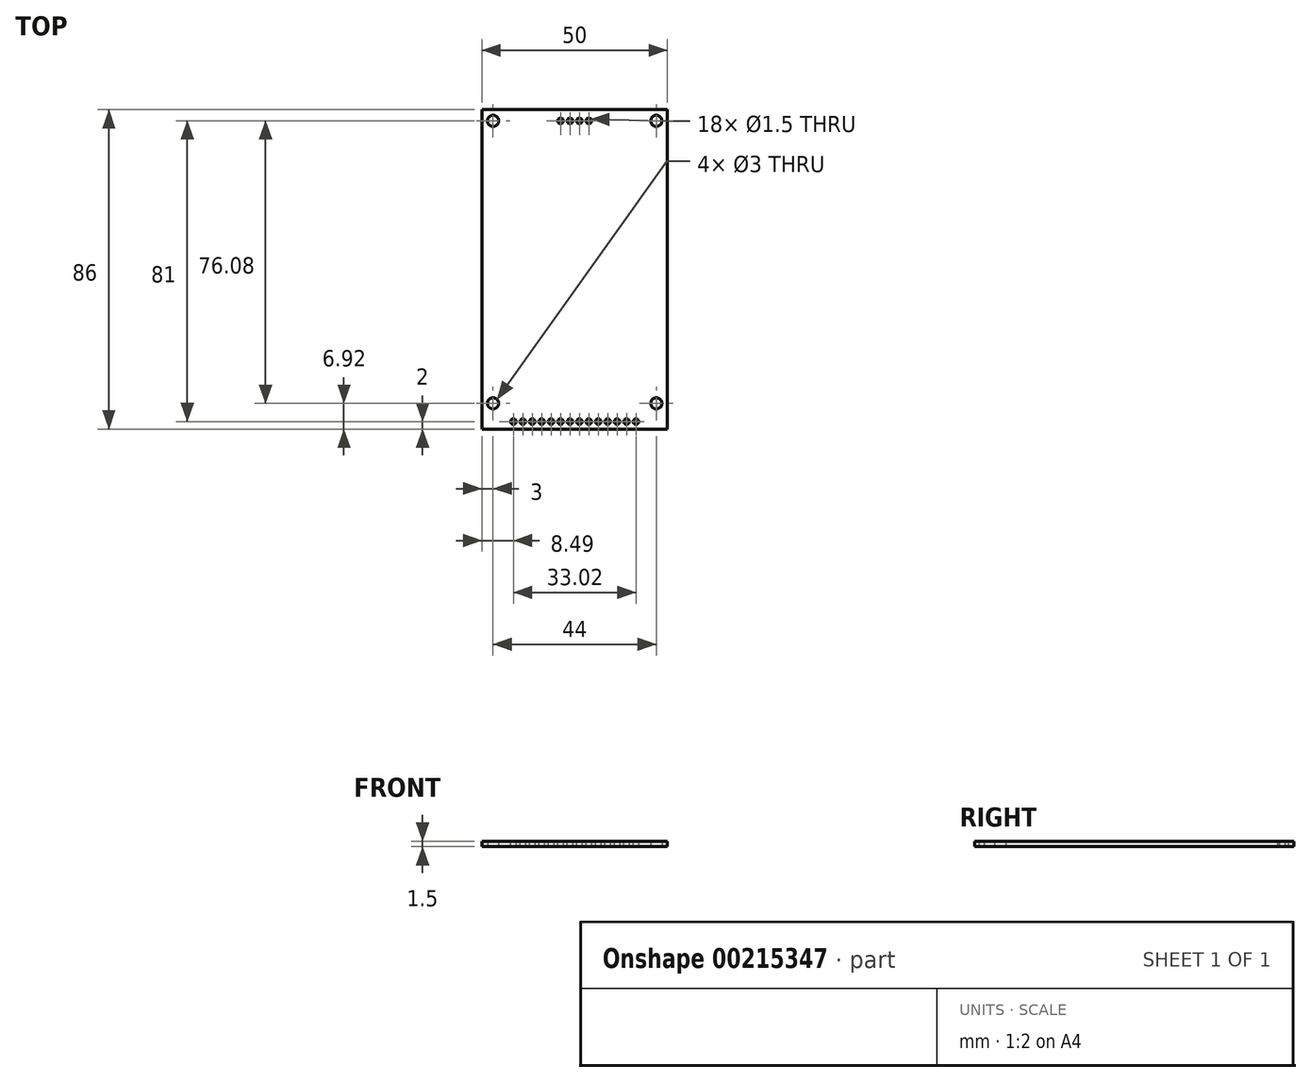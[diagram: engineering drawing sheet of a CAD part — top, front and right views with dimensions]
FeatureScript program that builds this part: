
annotation { "Feature Type Name" : "Feature", "Feature Type Description" : "" }
export const myFeature = defineFeature(function(context is Context, id is Id, definition is map)
    precondition{}
    {
        {
            var Q0;
            Q0=qCreatedBy(makeId("Top.planeOp"),FACE);
            var sketch = newSketch(context, id + "F0", { "sketchPlane" : qUnion([Q0])});
            skLineSegment(sketch, "E0.bottom", {"start": v(-25, 43) * mm, "end": v(25, 43) * mm});
            skLineSegment(sketch, "E0.top", {"start": v(-25, -43) * mm, "end": v(25, -43) * mm});
            skLineSegment(sketch, "E0.left", {"start": v(-25, 43) * mm, "end": v(-25, -43) * mm});
            skLineSegment(sketch, "E0.right", {"start": v(25, 43) * mm, "end": v(25, -43) * mm});
            skPoint(sketch, "E0.middle", {"position": v(0, 0) * mm});
            skCircle(sketch, "E1", {"center": v(-22, 40) * mm, "radius": 1.5 * mm});
            skCircle(sketch, "E2", {"center": v(22, 40) * mm, "radius": 1.5 * mm});
            skCircle(sketch, "E3", {"center": v(-22, -36.08) * mm, "radius": 1.5 * mm});
            skCircle(sketch, "E4", {"center": v(22, -36.08) * mm, "radius": 1.5 * mm});
            skSolve(sketch);
        }
        {
            var Q0;
            Q0 = qSketchRegion(id + "F0", true);
            extrude(context, id + "F1", {"entities" : qUnion([Q0]), "depth" : 1.5 * mm});
        }
        {
            var Q0;
            Q0=makeQuery(id+"F1.opExtrude","CAP_FACE",FACE,{"disambiguationData":[OSD([sQuery(id+"F0.wireOp",EDGE,"E0.bottom"),sQuery(id+"F0.wireOp",EDGE,"E0.top"),sQuery(id+"F0.wireOp",EDGE,"E0.left"),sQuery(id+"F0.wireOp",EDGE,"E0.right"),sQuery(id+"F0.wireOp",EDGE,"E1"),sQuery(id+"F0.wireOp",EDGE,"E2"),sQuery(id+"F0.wireOp",EDGE,"E3"),sQuery(id+"F0.wireOp",EDGE,"E4")])],"isStart":false});
            var sketch = newSketch(context, id + "F2", { "sketchPlane" : qUnion([Q0])});
            skCircle(sketch, "E5", {"center": v(-16.51, -41) * mm, "radius": 0.75 * mm});
            skCircle(sketch, "E6.1.0.0", {"center": v(-13.97, -41) * mm, "radius": 0.75 * mm});
            skCircle(sketch, "E6.2.0.0", {"center": v(-11.43, -41) * mm, "radius": 0.75 * mm});
            skCircle(sketch, "E6.3.0.0", {"center": v(-8.9, -41) * mm, "radius": 0.75 * mm});
            skCircle(sketch, "E6.4.0.0", {"center": v(-6.35, -41) * mm, "radius": 0.75 * mm});
            skCircle(sketch, "E6.5.0.0", {"center": v(-3.81, -41) * mm, "radius": 0.75 * mm});
            skCircle(sketch, "E6.6.0.0", {"center": v(-1.27, -41) * mm, "radius": 0.75 * mm});
            skCircle(sketch, "E6.7.0.0", {"center": v(1.27, -41) * mm, "radius": 0.75 * mm});
            skCircle(sketch, "E6.8.0.0", {"center": v(3.8, -41) * mm, "radius": 0.75 * mm});
            skCircle(sketch, "E6.9.0.0", {"center": v(6.35, -41) * mm, "radius": 0.75 * mm});
            skCircle(sketch, "E6.10.0.0", {"center": v(8.89, -41) * mm, "radius": 0.75 * mm});
            skCircle(sketch, "E6.11.0.0", {"center": v(11.43, -41) * mm, "radius": 0.75 * mm});
            skCircle(sketch, "E6.12.0.0", {"center": v(13.97, -41) * mm, "radius": 0.75 * mm});
            skCircle(sketch, "E6.13.0.0", {"center": v(16.51, -41) * mm, "radius": 0.75 * mm});
            skLineSegment(sketch, "E6.direction1", {"start": v(-16.51, -41) * mm, "end": v(-13.97, -41) * mm, "construction": true});
            skCircle(sketch, "E7", {"center": v(-3.8, 40) * mm, "radius": 0.75 * mm});
            skCircle(sketch, "E8.1.0.0", {"center": v(-1.27, 40) * mm, "radius": 0.75 * mm});
            skCircle(sketch, "E8.2.0.0", {"center": v(1.27, 40) * mm, "radius": 0.75 * mm});
            skCircle(sketch, "E8.3.0.0", {"center": v(3.81, 40) * mm, "radius": 0.75 * mm});
            skSolve(sketch);
        }
        {
            var Q0;
            Q0 = qSketchRegion(id + "F2", true);
            extrude(context, id + "F3", {"entities" : qUnion([Q0]), "operationType" : NewBodyOperationType.REMOVE, "endBound" : BoundingType.THROUGH_ALL, "oppositeDirection" : true, "depth" : 25 * mm});
        }
    });
